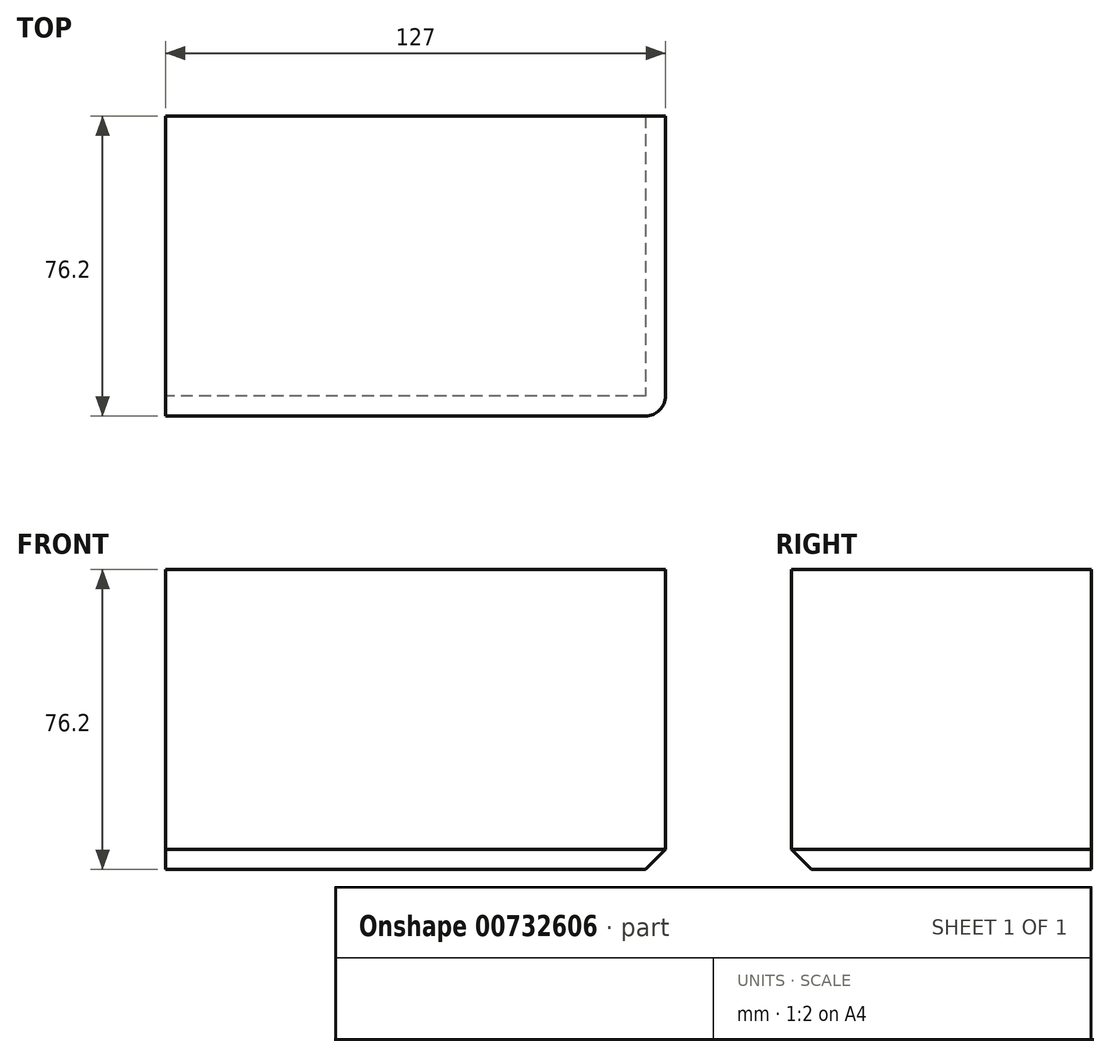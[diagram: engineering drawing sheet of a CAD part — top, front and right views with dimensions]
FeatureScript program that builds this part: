
annotation { "Feature Type Name" : "Feature", "Feature Type Description" : "" }
export const myFeature = defineFeature(function(context is Context, id is Id, definition is map)
    precondition{}
    {
        {
            var Q0;
            Q0=qCreatedBy(makeId("Top.planeOp"),FACE);
            var sketch = newSketch(context, id + "F0", { "sketchPlane" : qUnion([Q0])});
            skLineSegment(sketch, "E0.bottom", {"start": v(-83.21, -41.27) * mm, "end": v(43.79, -41.27) * mm});
            skLineSegment(sketch, "E0.top", {"start": v(-83.21, 34.93) * mm, "end": v(43.79, 34.93) * mm});
            skLineSegment(sketch, "E0.left", {"start": v(-83.21, -41.27) * mm, "end": v(-83.21, 34.93) * mm});
            skLineSegment(sketch, "E0.right", {"start": v(43.79, -41.27) * mm, "end": v(43.79, 34.93) * mm});
            skSolve(sketch);
        }
        {
            var Q0;
            Q0 = qSketchRegion(id + "F0", true);
            extrude(context, id + "F1", {"entities" : qUnion([Q0]), "depth" : 76.2 * mm, "offsetDistance" : 25.4 * mm});
        }
        {
            var Q0;
            Q0=makeQuery(id+"F1.opExtrude","CAP_FACE",FACE,{"disambiguationData":[OSD([sQuery(id+"F0.wireOp",EDGE,"E0.bottom"),sQuery(id+"F0.wireOp",EDGE,"E0.top"),sQuery(id+"F0.wireOp",EDGE,"E0.left"),sQuery(id+"F0.wireOp",EDGE,"E0.right")])],"isStart":false});
            var sketch = newSketch(context, id + "F2", { "sketchPlane" : qUnion([Q0])});
            skLineSegment(sketch, "E1.bottom", {"start": v(-7.01, -12.7) * mm, "end": v(-32.41, -12.7) * mm});
            skLineSegment(sketch, "E1.top", {"start": v(-7.01, 0) * mm, "end": v(-32.41, 0) * mm});
            skLineSegment(sketch, "E1.left", {"start": v(-7.01, -12.7) * mm, "end": v(-7.01, 0) * mm});
            skLineSegment(sketch, "E1.right", {"start": v(-32.41, -12.7) * mm, "end": v(-32.41, 0) * mm});
            skSolve(sketch);
        }
        {
            var Q0;
            Q0=makeQuery(id+"F2.imprint","IMPRINT",FACE,{"disambiguationData":[TD([[makeQuery(id+"F2.imprint","IMPRINT",EDGE,{"derivedFrom":sQuery(id+"F2.wireOp",EDGE,"E1.bottom")}),-1.0]])]});
            extrude(context, id + "F3", {"entities" : qUnion([Q0]), "operationType" : NewBodyOperationType.ADD, "oppositeDirection" : true, "depth" : 12.7 * mm, "offsetDistance" : 25.4 * mm});
        }
        {
            var Q0;
            Q0=makeQuery(id+"F1.opExtrude","SWEPT_EDGE",EDGE,{"disambiguationData":[OSD([sQuery(id+"F0.wireOp",EDGE,"E0.bottom"),sQuery(id+"F0.wireOp",EDGE,"E0.right")])]});
            fillet(context, id + "F4", {"entities" : qUnion([Q0]), "radius" : 5.08 * mm, "tangentPropagation" : true, "allowEdgeOverflow" : false});
        }
        {
            var Q0;
            Q0=makeQuery(id+"F1.opExtrude","CAP_EDGE",EDGE,{"disambiguationData":[OSD([sQuery(id+"F0.wireOp",EDGE,"E0.bottom")])],"isStart":true});
            chamfer(context, id + "F5", {"entities" : qUnion([Q0]), "width" : 5.08 * mm, "tangentPropagation" : true});
        }
    });
